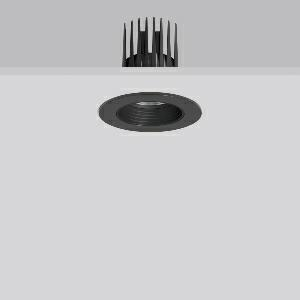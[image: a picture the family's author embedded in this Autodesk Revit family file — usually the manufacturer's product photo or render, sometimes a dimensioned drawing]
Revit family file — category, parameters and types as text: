
# Revit family: heledon_mini_e_901744_003_3_7cd7
name_source: partatom
category: Lighting Fixtures
units: mm (PartAtom-declared; Revit-internal decimal feet)

## family parameters
Cut with Voids When Loaded = No
Host = Face
Light Source = No
Part Type = Normal
Room Calculation Point = No
Round Connector Dimension = Use Diameter
Shared = No

## types (1)
- HELEDON mini E (1 x LED Modul 935, 2150 lm, 3500)
    Apparent Load = 20 VA
    Approval mark = CE
    CIE Flux Codes = 96 100 100 100 100
    Color Rendering = 92
    Color Temperature = 3500
    Default Elevation = 1800 mm
    Description = Series: HELEDON mini
Round recessed downlight. Housing: die-cast aluminium, powder-coated. Black plastic ring and recessed LED to prevent glare from the side. Optical assembly with lens made of plastic (polycarbonate) for the best homogeneous light distribution - can be changed without tools. Best colour rendering index Ra>90. Suitable for Recessed ceiling mounting. Installation without tools thanks to spring fastening system. Including separate LED converter with connecting cable 600 mm.High quality converter without flickering and stroboscopic effect. Through-wiring box (5 pole) available as accessory. The following accessories can be mounted without use of tools: interchangeable lenses, decorative glasses, honeycomb louvre, clear and frosted diffusers, white interchangeable plastic ring. 
Colour: deep black, matt (RAL 9005)
Diameter: 124 mm
Height: 3 mm
Cut-out diameter: 114 mm
Recess height: 170 mm
Luminaire: recess height: 120 mm
Lamp: LED
Socket: without socket
Colour temperature: 3500K
Colour rendering index (CRI): 92
System power: 20 W
Rated luminous flux: 2150 lm
Luminous efficiency: 108 lm/W
Control gear: Regulated power supply
Protection class: II
Type of protection: IP 20
    Height = 0 mm  [stored 0 ft]
    Lamp = 1 x LED Modul 935
    Lamp Light Flux = 2150 lm
    Lamp count = 1
    Length = 124 mm  [stored 0.406824 ft]
    Lifetime = 50000 h
    Luminous efficacy = 108 lm/W
    Manufacturer = RZB
    ModVariant = No
    Model = 901744.003.3
    Mounting Place = Ceiling
    Mounting Type = Recessed
    Number of Poles = 1
    OnlyDefault = Yes
    Power Factor = 1
    Product Name = HELEDON mini E
    Product group = Recessed downlights
    ProductGroupID = 402
    Protection Class = Protection class II
    Protection Degree = IP 20
    RLX_Detail_Level = 1
    RLX_Emergency_Light_Flux = 0 lm
    RLX_Emergency_Type = 0
    RLX_Emergency_Type_DB = No
    RlxData = <blob elided: 124985 chars, md5=4d2d8d2e>
    Socket = socket
    Standby Power = 0 W
    System Light Flux = 2150 lm
    System Power = 20 W
    Type Comments = Product without accessories
    Type Image = 901656.003.jpg
    URL = http://relux.com
    VarID = ---
    Voltage = 230 V
    Voltage Range = 220-240 V
    Weight = 0.00 kg
    Width = 0 mm  [stored 0 ft]

note: [stored X ft] marks values corroborated as IEEE doubles in the binary element streams (Revit-internal decimal feet)

## geometry (parser evidence)
native form markers: Blend x4, Sweep x11
no freeform markers — native parametric forms only
